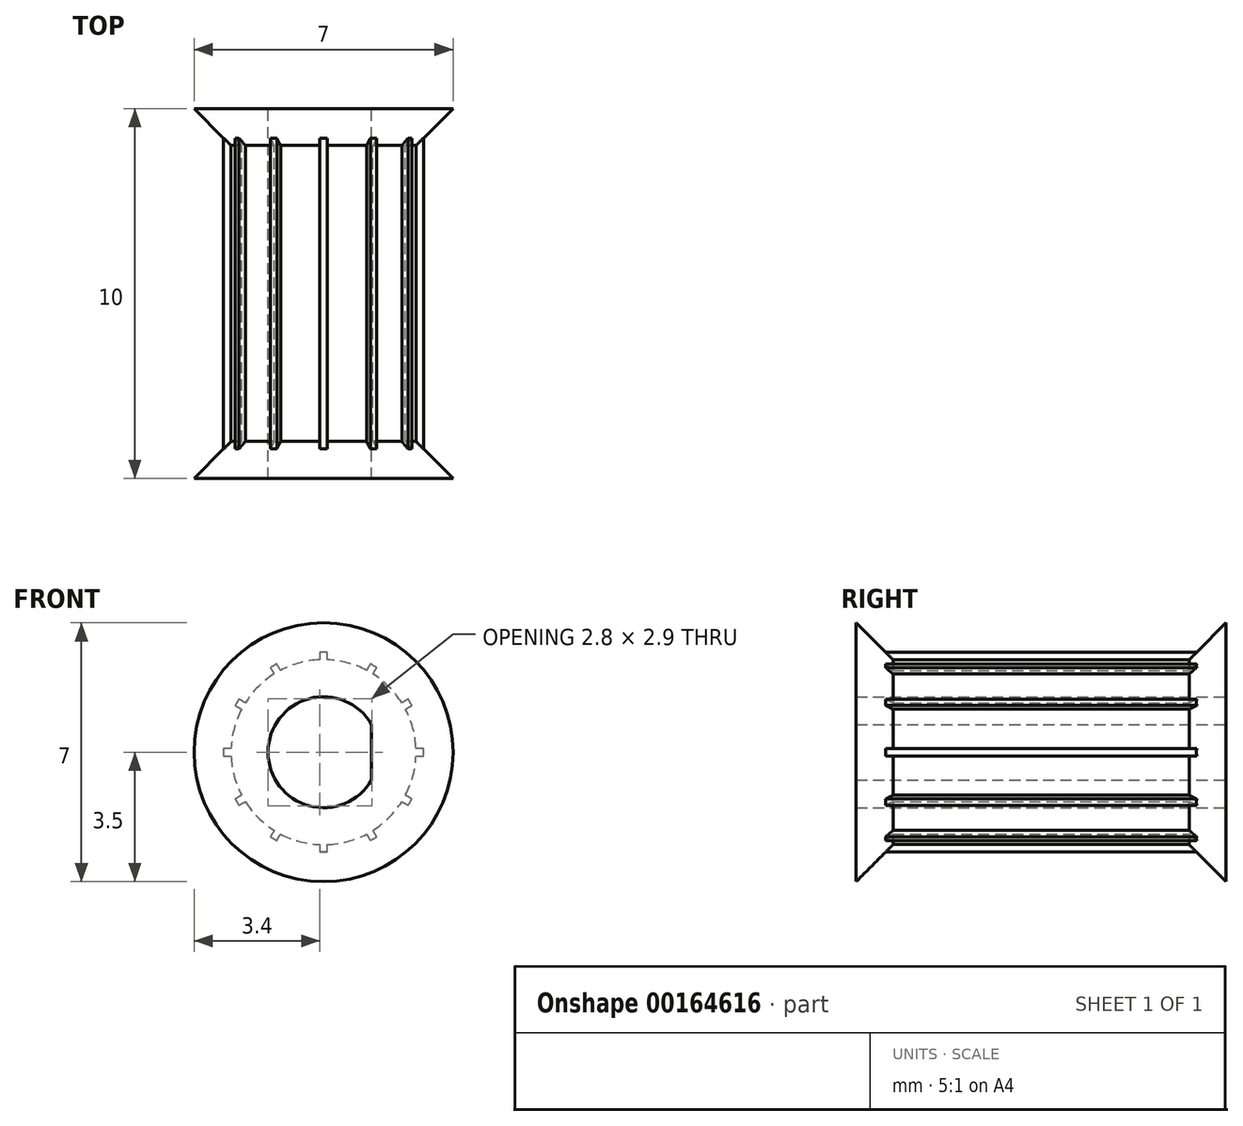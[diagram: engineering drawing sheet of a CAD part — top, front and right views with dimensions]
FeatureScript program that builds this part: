
annotation { "Feature Type Name" : "Feature", "Feature Type Description" : "" }
export const myFeature = defineFeature(function(context is Context, id is Id, definition is map)
    precondition{}
    {
        {
            var Q0;
            Q0=qCreatedBy(makeId("Front.planeOp"),FACE);
            var sketch = newSketch(context, id + "F0", { "sketchPlane" : qUnion([Q0])});
            skCircle(sketch, "E0", {"center": v(0, 0) * mm, "radius": 2.5 * mm});
            skArc(sketch, "E1", {"start": v(1.3, 0.75) * mm, "mid": v(-1.5, 0) * mm, "end": v(1.3, -0.75) * mm});
            skLineSegment(sketch, "E2", {"start": v(1.3, 0.75) * mm, "end": v(1.3, -0.75) * mm});
            skLineSegment(sketch, "E3", {"start": v(-0.1, 2.5) * mm, "end": v(-0.1, 2.7) * mm});
            skLineSegment(sketch, "E4", {"start": v(-0.1, 2.7) * mm, "end": v(0.1, 2.7) * mm});
            skLineSegment(sketch, "E5", {"start": v(0.1, 2.7) * mm, "end": v(0.1, 2.5) * mm});
            skLineSegment(sketch, "E6.1.0", {"start": v(-1.26, 2.39) * mm, "end": v(-1.16, 2.21) * mm});
            skLineSegment(sketch, "E6.1.1", {"start": v(-1.44, 2.29) * mm, "end": v(-1.26, 2.39) * mm});
            skLineSegment(sketch, "E6.1.2", {"start": v(-1.34, 2.11) * mm, "end": v(-1.44, 2.29) * mm});
            skLineSegment(sketch, "E6.2.0", {"start": v(-2.29, 1.44) * mm, "end": v(-2.11, 1.34) * mm});
            skLineSegment(sketch, "E6.2.1", {"start": v(-2.39, 1.26) * mm, "end": v(-2.29, 1.44) * mm});
            skLineSegment(sketch, "E6.2.2", {"start": v(-2.21, 1.16) * mm, "end": v(-2.39, 1.26) * mm});
            skLineSegment(sketch, "E6.3.0", {"start": v(-2.7, 0.1) * mm, "end": v(-2.5, 0.1) * mm});
            skLineSegment(sketch, "E6.3.1", {"start": v(-2.7, -0.1) * mm, "end": v(-2.7, 0.1) * mm});
            skLineSegment(sketch, "E6.3.2", {"start": v(-2.5, -0.1) * mm, "end": v(-2.7, -0.1) * mm});
            skLineSegment(sketch, "E6.4.0", {"start": v(-2.39, -1.26) * mm, "end": v(-2.21, -1.16) * mm});
            skLineSegment(sketch, "E6.4.1", {"start": v(-2.29, -1.44) * mm, "end": v(-2.39, -1.26) * mm});
            skLineSegment(sketch, "E6.4.2", {"start": v(-2.11, -1.34) * mm, "end": v(-2.29, -1.44) * mm});
            skLineSegment(sketch, "E6.5.0", {"start": v(-1.44, -2.29) * mm, "end": v(-1.34, -2.11) * mm});
            skLineSegment(sketch, "E6.5.1", {"start": v(-1.26, -2.39) * mm, "end": v(-1.44, -2.29) * mm});
            skLineSegment(sketch, "E6.5.2", {"start": v(-1.16, -2.21) * mm, "end": v(-1.26, -2.39) * mm});
            skLineSegment(sketch, "E6.6.0", {"start": v(-0.1, -2.7) * mm, "end": v(-0.1, -2.5) * mm});
            skLineSegment(sketch, "E6.6.1", {"start": v(0.1, -2.7) * mm, "end": v(-0.1, -2.7) * mm});
            skLineSegment(sketch, "E6.6.2", {"start": v(0.1, -2.5) * mm, "end": v(0.1, -2.7) * mm});
            skLineSegment(sketch, "E6.7.0", {"start": v(1.26, -2.39) * mm, "end": v(1.16, -2.21) * mm});
            skLineSegment(sketch, "E6.7.1", {"start": v(1.44, -2.29) * mm, "end": v(1.26, -2.39) * mm});
            skLineSegment(sketch, "E6.7.2", {"start": v(1.34, -2.11) * mm, "end": v(1.44, -2.29) * mm});
            skLineSegment(sketch, "E6.8.0", {"start": v(2.29, -1.44) * mm, "end": v(2.11, -1.34) * mm});
            skLineSegment(sketch, "E6.8.1", {"start": v(2.39, -1.26) * mm, "end": v(2.29, -1.44) * mm});
            skLineSegment(sketch, "E6.8.2", {"start": v(2.21, -1.16) * mm, "end": v(2.39, -1.26) * mm});
            skLineSegment(sketch, "E6.9.0", {"start": v(2.7, -0.1) * mm, "end": v(2.5, -0.1) * mm});
            skLineSegment(sketch, "E6.9.1", {"start": v(2.7, 0.1) * mm, "end": v(2.7, -0.1) * mm});
            skLineSegment(sketch, "E6.9.2", {"start": v(2.5, 0.1) * mm, "end": v(2.7, 0.1) * mm});
            skLineSegment(sketch, "E6.10.0", {"start": v(2.39, 1.26) * mm, "end": v(2.21, 1.16) * mm});
            skLineSegment(sketch, "E6.10.1", {"start": v(2.29, 1.44) * mm, "end": v(2.39, 1.26) * mm});
            skLineSegment(sketch, "E6.10.2", {"start": v(2.11, 1.34) * mm, "end": v(2.29, 1.44) * mm});
            skLineSegment(sketch, "E6.11.0", {"start": v(1.44, 2.29) * mm, "end": v(1.34, 2.11) * mm});
            skLineSegment(sketch, "E6.11.1", {"start": v(1.26, 2.39) * mm, "end": v(1.44, 2.29) * mm});
            skLineSegment(sketch, "E6.11.2", {"start": v(1.16, 2.21) * mm, "end": v(1.26, 2.39) * mm});
            skSolve(sketch);
        }
        {
            var Q0;
            {var subQ0=sQuery(id+"F0.wireOp",EDGE,"E3");Q0=makeQuery(id+"F0.imprint","IMPRINT",FACE,{"disambiguationData":[TD([[makeQuery(id+"F0.imprint","IMPRINT",EDGE,{"derivedFrom":subQ0}),-1.0]])]});}
            var Q1;
            {var subQ0=sQuery(id+"F0.wireOp",EDGE,"E6.1.0");Q1=makeQuery(id+"F0.imprint","IMPRINT",FACE,{"disambiguationData":[TD([[makeQuery(id+"F0.imprint","IMPRINT",EDGE,{"derivedFrom":subQ0}),-1.0]])]});}
            var Q2;
            {var subQ0=sQuery(id+"F0.wireOp",EDGE,"E6.2.0");Q2=makeQuery(id+"F0.imprint","IMPRINT",FACE,{"disambiguationData":[TD([[makeQuery(id+"F0.imprint","IMPRINT",EDGE,{"derivedFrom":subQ0}),-1.0]])]});}
            var Q3;
            {var subQ0=sQuery(id+"F0.wireOp",EDGE,"E6.3.0");Q3=makeQuery(id+"F0.imprint","IMPRINT",FACE,{"disambiguationData":[TD([[makeQuery(id+"F0.imprint","IMPRINT",EDGE,{"derivedFrom":subQ0}),-1.0]])]});}
            var Q4;
            {var subQ0=sQuery(id+"F0.wireOp",EDGE,"E6.4.0");Q4=makeQuery(id+"F0.imprint","IMPRINT",FACE,{"disambiguationData":[TD([[makeQuery(id+"F0.imprint","IMPRINT",EDGE,{"derivedFrom":subQ0}),-1.0]])]});}
            var Q5;
            {var subQ0=sQuery(id+"F0.wireOp",EDGE,"E6.5.0");Q5=makeQuery(id+"F0.imprint","IMPRINT",FACE,{"disambiguationData":[TD([[makeQuery(id+"F0.imprint","IMPRINT",EDGE,{"derivedFrom":subQ0}),-1.0]])]});}
            var Q6;
            {var subQ0=sQuery(id+"F0.wireOp",EDGE,"E6.6.0");Q6=makeQuery(id+"F0.imprint","IMPRINT",FACE,{"disambiguationData":[TD([[makeQuery(id+"F0.imprint","IMPRINT",EDGE,{"derivedFrom":subQ0}),-1.0]])]});}
            var Q7;
            {var subQ0=sQuery(id+"F0.wireOp",EDGE,"E6.7.0");Q7=makeQuery(id+"F0.imprint","IMPRINT",FACE,{"disambiguationData":[TD([[makeQuery(id+"F0.imprint","IMPRINT",EDGE,{"derivedFrom":subQ0}),-1.0]])]});}
            var Q8;
            {var subQ0=sQuery(id+"F0.wireOp",EDGE,"E6.8.0");Q8=makeQuery(id+"F0.imprint","IMPRINT",FACE,{"disambiguationData":[TD([[makeQuery(id+"F0.imprint","IMPRINT",EDGE,{"derivedFrom":subQ0}),-1.0]])]});}
            var Q9;
            {var subQ0=sQuery(id+"F0.wireOp",EDGE,"E6.9.0");Q9=makeQuery(id+"F0.imprint","IMPRINT",FACE,{"disambiguationData":[TD([[makeQuery(id+"F0.imprint","IMPRINT",EDGE,{"derivedFrom":subQ0}),-1.0]])]});}
            var Q10;
            {var subQ0=sQuery(id+"F0.wireOp",EDGE,"E6.10.0");Q10=makeQuery(id+"F0.imprint","IMPRINT",FACE,{"disambiguationData":[TD([[makeQuery(id+"F0.imprint","IMPRINT",EDGE,{"derivedFrom":subQ0}),-1.0]])]});}
            var Q11;
            {var subQ0=sQuery(id+"F0.wireOp",EDGE,"E6.11.0");Q11=makeQuery(id+"F0.imprint","IMPRINT",FACE,{"disambiguationData":[TD([[makeQuery(id+"F0.imprint","IMPRINT",EDGE,{"derivedFrom":subQ0}),-1.0]])]});}
            var Q12;
            Q12=makeQuery(id+"F0.imprint","IMPRINT",FACE,{"disambiguationData":[TD([[makeQuery(id+"F0.imprint","IMPRINT",EDGE,{"derivedFrom":sQuery(id+"F0.wireOp",EDGE,"E1")}),-1.0]])]});
            extrude(context, id + "F1", {"entities" : qUnion([Q0, Q1, Q2, Q3, Q4, Q5, Q6, Q7, Q8, Q9, Q10, Q11, Q12]), "depth" : 10 * mm});
        }
        {
            var Q0;
            Q0=qCreatedBy(makeId("Right.planeOp"),FACE);
            var sketch = newSketch(context, id + "F2", { "sketchPlane" : qUnion([Q0])});
            skLineSegment(sketch, "E7", {"start": v(-10, 3.5) * mm, "end": v(-10, 2.5) * mm});
            skLineSegment(sketch, "E8", {"start": v(-10, 2.5) * mm, "end": v(-9, 2.5) * mm});
            skLineSegment(sketch, "E9", {"start": v(-9, 2.5) * mm, "end": v(-10, 3.5) * mm});
            skLineSegment(sketch, "E10", {"start": v(0, 2.5) * mm, "end": v(0, 3.5) * mm});
            skLineSegment(sketch, "E11", {"start": v(0, 3.5) * mm, "end": v(-1, 2.5) * mm});
            skLineSegment(sketch, "E12", {"start": v(-1, 2.5) * mm, "end": v(0, 2.5) * mm});
            skLineSegment(sketch, "E13", {"start": v(-12.27, 0) * mm, "end": v(1.77, 0) * mm, "construction": true});
            skSolve(sketch);
        }
        {
            var Q0;
            Q0=makeQuery(id+"F2.imprint","IMPRINT",FACE,{"disambiguationData":[TD([[makeQuery(id+"F2.imprint","IMPRINT",EDGE,{"derivedFrom":sQuery(id+"F2.wireOp",EDGE,"E7")}),1.0]])]});
            var Q1;
            Q1=makeQuery(id+"F2.imprint","IMPRINT",FACE,{"disambiguationData":[TD([[makeQuery(id+"F2.imprint","IMPRINT",EDGE,{"derivedFrom":sQuery(id+"F2.wireOp",EDGE,"E10")}),1.0]])]});
            var Q2;
            Q2=sQuery(id+"F2.wireOp",EDGE,"E13");
            revolve(context, id + "F3", {"operationType" : NewBodyOperationType.ADD, "entities" : qUnion([Q0, Q1]), "axis" : qUnion([Q2]), "revolveType" : RevolveType.FULL});
        }
    });
